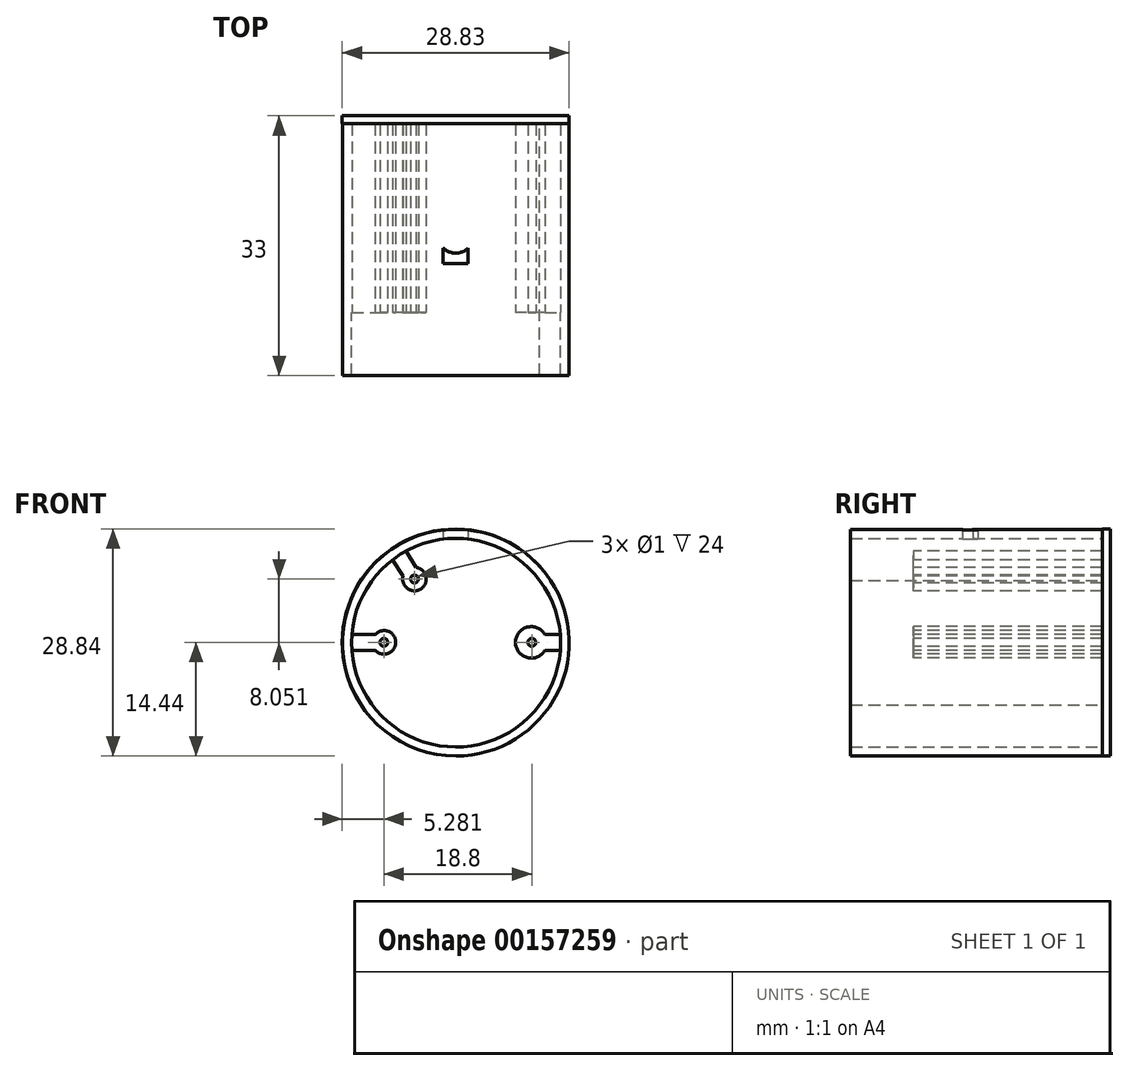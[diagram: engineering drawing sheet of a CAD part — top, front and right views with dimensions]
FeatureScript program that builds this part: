
annotation { "Feature Type Name" : "Feature", "Feature Type Description" : "" }
export const myFeature = defineFeature(function(context is Context, id is Id, definition is map)
    precondition{}
    {
        {
            var Q0;
            Q0=qCreatedBy(makeId("Front.planeOp"),FACE);
            var sketch = newSketch(context, id + "F0", { "sketchPlane" : qUnion([Q0])});
            skCircle(sketch, "E0.0", {"center": v(0.03, -0.04) * mm, "radius": 9.15 * mm, "construction": true});
            skCircle(sketch, "E1.0", {"center": v(0.03, -0.04) * mm, "radius": 9.65 * mm, "construction": true});
            skCircle(sketch, "E2.0", {"center": v(9.6, 0) * mm, "radius": 2 * mm});
            skCircle(sketch, "E3", {"center": v(-9.12, 0) * mm, "radius": 0.5 * mm});
            skCircle(sketch, "E4", {"center": v(9.68, 0) * mm, "radius": 0.5 * mm});
            skCircle(sketch, "E5", {"center": v(-5.23, 8.05) * mm, "radius": 0.5 * mm});
            skCircle(sketch, "E6", {"center": v(-5.23, 8.05) * mm, "radius": 1.5 * mm});
            skArc(sketch, "E7", {"start": v(10.68, 7.85) * mm, "mid": v(-13.22, -0.04) * mm, "end": v(10.68, -7.93) * mm});
            skArc(sketch, "E8.trimOffspring", {"start": v(10.68, -7.93) * mm, "mid": v(13.34, -0.04) * mm, "end": v(10.68, 7.85) * mm});
            skCircle(sketch, "E9", {"center": v(0.03, -0.04) * mm, "radius": 14.4 * mm});
            skLineSegment(sketch, "E10.trimOffspring", {"start": v(-6.68, 8.44) * mm, "end": v(-8, 10.5) * mm});
            skLineSegment(sketch, "E11.trimOffspring", {"start": v(-5, 9.53) * mm, "end": v(-6.32, 11.59) * mm});
            skLineSegment(sketch, "E12.0", {"start": v(-13.2, -1) * mm, "end": v(-10.83, -1) * mm});
            skLineSegment(sketch, "E13.0", {"start": v(-13.2, 1) * mm, "end": v(-10.83, 1) * mm});
            skLineSegment(sketch, "E14.0", {"start": v(11.33, 1) * mm, "end": v(13.25, 1) * mm});
            skLineSegment(sketch, "E15.0", {"start": v(11.33, -1) * mm, "end": v(13.25, -1) * mm});
            skPoint(sketch, "E16.orphan", {"position": v(-13.22, -0.04) * mm});
            skPoint(sketch, "E17.orphan", {"position": v(13.34, -0.04) * mm});
            skCircle(sketch, "E18", {"center": v(-9.1, 0) * mm, "radius": 1.5 * mm});
            skLineSegment(sketch, "E19", {"start": v(-10.83, 1) * mm, "end": v(-10.22, 1) * mm});
            skLineSegment(sketch, "E20", {"start": v(-10.83, -1) * mm, "end": v(-10.22, -1) * mm});
            skLineSegment(sketch, "E21", {"start": v(13.25, 1) * mm, "end": v(13.3, 1) * mm});
            skLineSegment(sketch, "E22", {"start": v(13.25, -1) * mm, "end": v(13.3, -1) * mm});
            skSolve(sketch);
        }
        {
            var Q0;
            Q0=makeQuery(id+"F0.imprint","IMPRINT",FACE,{"disambiguationData":[TD([[makeQuery(id+"F0.imprint","IMPRINT",EDGE,{"derivedFrom":sQuery(id+"F0.wireOp",EDGE,"E9")}),1.0]])]});
            extrude(context, id + "F1", {"entities" : qUnion([Q0]), "depth" : 8 * mm});
        }
        {
            var Q0;
            {var subQ0=sQuery(id+"F0.wireOp",EDGE,"E12.0");var subQ1=sQuery(id+"F0.wireOp",EDGE,"f3b392bf-b8ac-4f1c-9f60-57eba29f36f3.0");var subQ2=makeQuery(id+"F0.imprint","INTERSECT",VERTEX,{"derivedFrom":[subQ1,subQ0]});Q0=makeQuery(id+"F0.imprint","IMPRINT",FACE,{"disambiguationData":[TD([[makeQuery(id+"F0.imprint","IMPRINT",EDGE,{"disambiguationData":[TD([[subQ2,1.0]])],"derivedFrom":subQ1}),-1.0]])]});}
            var Q1;
            Q1=makeQuery(id+"F0.imprint","IMPRINT",FACE,{"disambiguationData":[TD([[makeQuery(id+"F0.imprint","IMPRINT",EDGE,{"derivedFrom":sQuery(id+"F0.wireOp",EDGE,"E3")}),-1.0]])]});
            var Q2;
            {var subQ0=sQuery(id+"F0.wireOp",EDGE,"E10.trimOffspring");Q2=makeQuery(id+"F0.imprint","IMPRINT",FACE,{"disambiguationData":[TD([[makeQuery(id+"F0.imprint","IMPRINT",EDGE,{"derivedFrom":subQ0}),-1.0]])]});}
            var Q3;
            Q3=makeQuery(id+"F0.imprint","IMPRINT",FACE,{"disambiguationData":[TD([[makeQuery(id+"F0.imprint","IMPRINT",EDGE,{"derivedFrom":sQuery(id+"F0.wireOp",EDGE,"E9")}),1.0]])]});
            var Q4;
            {var subQ0=sQuery(id+"F0.wireOp",EDGE,"E14.0");var subQ1=sQuery(id+"F0.wireOp",EDGE,"E2.0");var subQ2=makeQuery(id+"F0.imprint","INTERSECT",VERTEX,{"derivedFrom":[subQ1,subQ0]});Q4=makeQuery(id+"F0.imprint","IMPRINT",FACE,{"disambiguationData":[TD([[makeQuery(id+"F0.imprint","IMPRINT",EDGE,{"disambiguationData":[TD([[subQ2,1.0]])],"derivedFrom":subQ1}),-1.0]])]});}
            var Q5;
            Q5=makeQuery(id+"F0.imprint","IMPRINT",FACE,{"disambiguationData":[TD([[makeQuery(id+"F0.imprint","IMPRINT",EDGE,{"derivedFrom":sQuery(id+"F0.wireOp",EDGE,"E4")}),-1.0]])]});
            var Q6;
            Q6=makeQuery(id+"F0.imprint","IMPRINT",FACE,{"disambiguationData":[TD([[makeQuery(id+"F0.imprint","IMPRINT",EDGE,{"derivedFrom":sQuery(id+"F0.wireOp",EDGE,"E5")}),-1.0]])]});
            var Q7;
            {var subQ0=sQuery(id+"F0.wireOp",EDGE,"E19");Q7=makeQuery(id+"F0.imprint","IMPRINT",FACE,{"disambiguationData":[TD([[makeQuery(id+"F0.imprint","IMPRINT",EDGE,{"derivedFrom":subQ0}),-1.0]])]});}
            extrude(context, id + "F2", {"entities" : qUnion([Q0, Q1, Q2, Q3, Q4, Q5, Q6, Q7]), "operationType" : NewBodyOperationType.ADD, "oppositeDirection" : true, "depth" : 24 * mm});
        }
        {
            var Q0;
            Q0=qCreatedBy(makeId("Top.planeOp"),FACE);
            var sketch = newSketch(context, id + "F3", { "sketchPlane" : qUnion([Q0])});
            skCircle(sketch, "E23", {"center": v(0, 9.86) * mm, "radius": 2.3 * mm});
            skLineSegment(sketch, "E24.0", {"start": v(1.6, 11.5) * mm, "end": v(1.6, 13.46) * mm});
            skLineSegment(sketch, "E25.0", {"start": v(-1.6, 11.5) * mm, "end": v(-1.6, 13.46) * mm});
            skLineSegment(sketch, "E26", {"start": v(-1.6, 13.46) * mm, "end": v(1.6, 13.46) * mm});
            skLineSegment(sketch, "E27.MirrorCS", {"start": v(1.6, 13.46) * mm, "end": v(-1.6, 13.46) * mm});
            skLineSegment(sketch, "E28.0", {"start": v(-1.6, 8.2) * mm, "end": v(-1.6, 6.26) * mm});
            skLineSegment(sketch, "E29.0", {"start": v(1.6, 8.2) * mm, "end": v(1.6, 6.26) * mm});
            skLineSegment(sketch, "E30", {"start": v(-1.6, 6.26) * mm, "end": v(1.6, 6.26) * mm});
            skSolve(sketch);
        }
        {
            var Q0;
            {var subQ0=sQuery(id+"F3.wireOp",EDGE,"E28.0");Q0=makeQuery(id+"F3.imprint","IMPRINT",FACE,{"disambiguationData":[TD([[makeQuery(id+"F3.imprint","IMPRINT",EDGE,{"derivedFrom":subQ0}),1.0]])]});}
            var Q1;
            {var subQ0=sQuery(id+"F3.wireOp",EDGE,"E23");var subQ1=makeQuery(id+"F3.imprint","INTERSECT",VERTEX,{"derivedFrom":[subQ0,sQuery(id+"F3.wireOp",EDGE,"E24.0")]});Q1=makeQuery(id+"F3.imprint","IMPRINT",FACE,{"disambiguationData":[TD([[makeQuery(id+"F3.imprint","IMPRINT",EDGE,{"disambiguationData":[TD([[subQ1,1.0]])],"derivedFrom":subQ0}),-1.0]])]});}
            var Q2;
            Q2=makeQuery(id+"F3.imprint","IMPRINT",FACE,{"disambiguationData":[TD([[makeQuery(id+"F3.imprint","IMPRINT",EDGE,{"derivedFrom":sQuery(id+"F3.wireOp",EDGE,"E27.MirrorCS")}),1.0]])]});
            extrude(context, id + "F4", {"entities" : qUnion([Q0, Q1, Q2]), "operationType" : NewBodyOperationType.REMOVE, "depth" : 25 * mm});
        }
        {
            var Q0;
            Q0=makeQuery(id+"F2.opExtrude","CAP_FACE",FACE,{"disambiguationData":[OSD([sQuery(id+"F0.wireOp",EDGE,"f3b392bf-b8ac-4f1c-9f60-57eba29f36f3.0"),sQuery(id+"F0.wireOp",EDGE,"E2.0"),sQuery(id+"F0.wireOp",EDGE,"E3"),sQuery(id+"F0.wireOp",EDGE,"E4"),sQuery(id+"F0.wireOp",EDGE,"E5"),sQuery(id+"F0.wireOp",EDGE,"E6"),sQuery(id+"F0.wireOp",EDGE,"E7"),sQuery(id+"F0.wireOp",EDGE,"E8.trimOffspring"),sQuery(id+"F0.wireOp",EDGE,"E9"),sQuery(id+"F0.wireOp",EDGE,"E10.trimOffspring"),sQuery(id+"F0.wireOp",EDGE,"E11.trimOffspring"),sQuery(id+"F0.wireOp",EDGE,"E12.0"),sQuery(id+"F0.wireOp",EDGE,"E13.0"),sQuery(id+"F0.wireOp",EDGE,"E14.0"),sQuery(id+"F0.wireOp",EDGE,"E15.0")])],"isStart":false});
            var sketch = newSketch(context, id + "F5", { "sketchPlane" : qUnion([Q0])});
            skCircle(sketch, "E31", {"center": v(0, 0) * mm, "radius": 14.4 * mm});
            skSolve(sketch);
        }
        {
            var Q0;
            Q0 = qSketchRegion(id + "F5", true);
            extrude(context, id + "F6", {"entities" : qUnion([Q0]), "operationType" : NewBodyOperationType.ADD, "depth" : 1 * mm});
        }
    });
